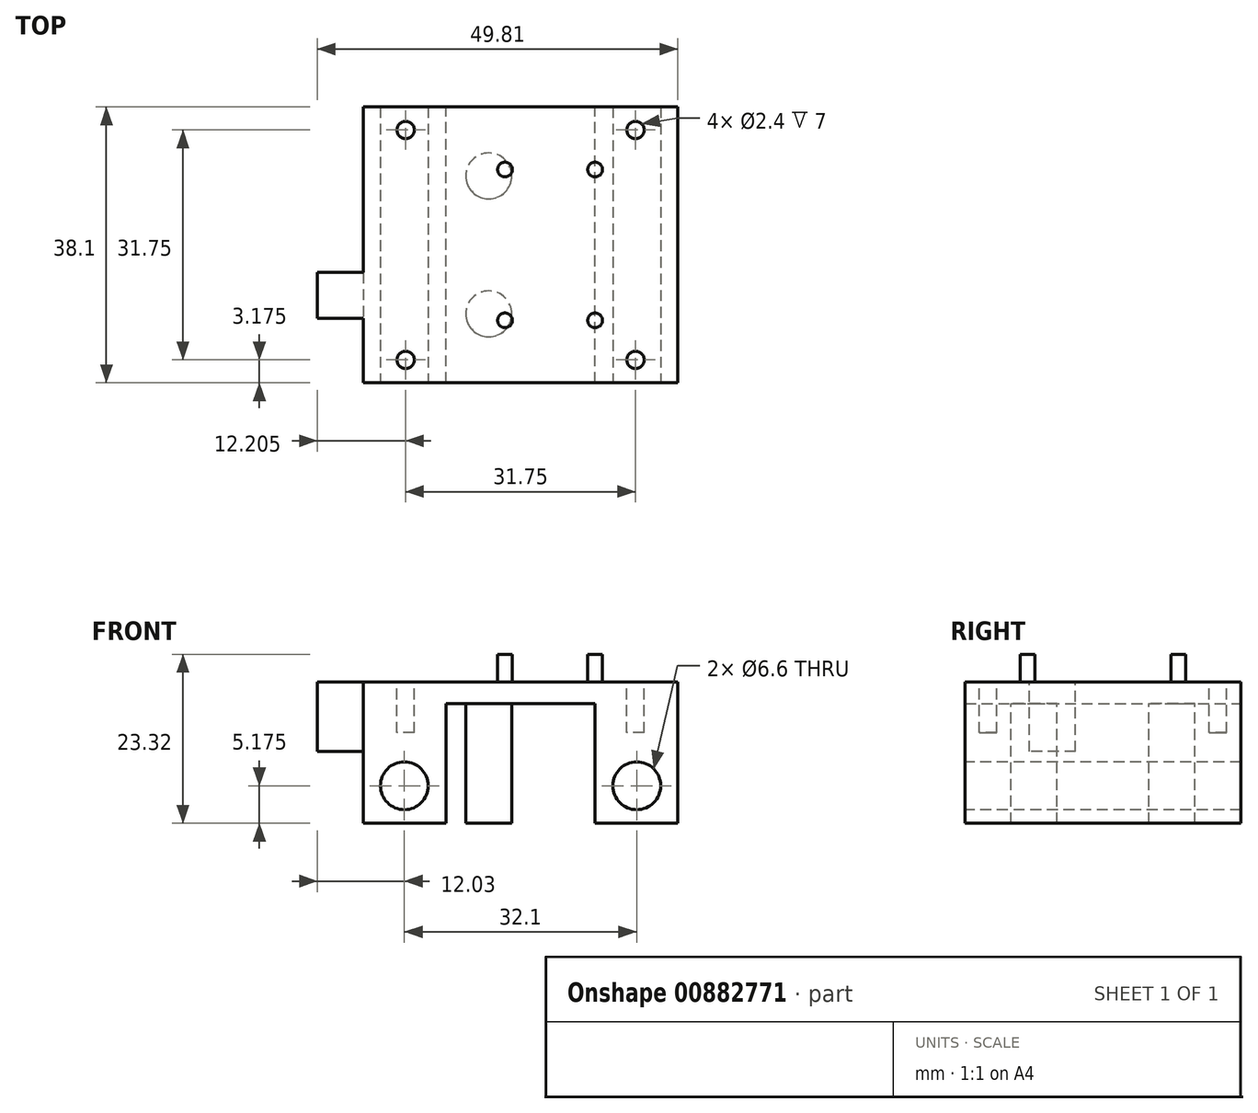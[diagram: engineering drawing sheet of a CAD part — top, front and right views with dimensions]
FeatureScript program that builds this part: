
annotation { "Feature Type Name" : "Feature", "Feature Type Description" : "" }
export const myFeature = defineFeature(function(context is Context, id is Id, definition is map)
    precondition{}
    {
        {
            var Q0;
            Q0=qCreatedBy(makeId("Top.planeOp"),FACE);
            var sketch = newSketch(context, id + "F0", { "sketchPlane" : qUnion([Q0])});
            skLineSegment(sketch, "E0.bottom", {"start": v(21.73, -19.05) * mm, "end": v(-21.73, -19.05) * mm});
            skLineSegment(sketch, "E0.top", {"start": v(21.73, 19.05) * mm, "end": v(-21.73, 19.05) * mm});
            skLineSegment(sketch, "E0.left", {"start": v(21.73, -19.05) * mm, "end": v(21.73, 19.05) * mm});
            skLineSegment(sketch, "E0.right", {"start": v(-21.73, -19.05) * mm, "end": v(-21.73, 19.05) * mm});
            skPoint(sketch, "E0.middle", {"position": v(0, 0) * mm});
            skSolve(sketch);
        }
        {
            var Q0;
            Q0 = qSketchRegion(id + "F0", true);
            extrude(context, id + "F1", {"entities" : qUnion([Q0]), "depth" : 3 * mm, "offsetDistance" : 25.4 * mm});
        }
        {
            var Q0;
            Q0=makeQuery(id+"F1.opExtrude","CAP_FACE",FACE,{"disambiguationData":[OSD([sQuery(id+"F0.wireOp",EDGE,"E0.bottom"),sQuery(id+"F0.wireOp",EDGE,"E0.top"),sQuery(id+"F0.wireOp",EDGE,"E0.left"),sQuery(id+"F0.wireOp",EDGE,"E0.right")])],"isStart":true});
            var sketch = newSketch(context, id + "F2", { "sketchPlane" : qUnion([Q0])});
            skLineSegment(sketch, "E1.bottom", {"start": v(-21.73, 19.05) * mm, "end": v(-10.3, 19.05) * mm});
            skLineSegment(sketch, "E1.top", {"start": v(-21.73, -19.05) * mm, "end": v(-10.3, -19.05) * mm});
            skLineSegment(sketch, "E1.left", {"start": v(-21.73, 19.05) * mm, "end": v(-21.73, -19.05) * mm});
            skLineSegment(sketch, "E1.right", {"start": v(-10.3, 19.05) * mm, "end": v(-10.3, -19.05) * mm});
            skLineSegment(sketch, "E2.MirrorCS", {"start": v(10.3, 19.05) * mm, "end": v(10.3, -19.05) * mm});
            skLineSegment(sketch, "E3.MirrorCS", {"start": v(21.73, 19.05) * mm, "end": v(10.3, 19.05) * mm});
            skLineSegment(sketch, "E4.MirrorCS", {"start": v(21.73, 19.05) * mm, "end": v(21.73, -19.05) * mm});
            skLineSegment(sketch, "E5.MirrorCS", {"start": v(21.73, -19.05) * mm, "end": v(10.3, -19.05) * mm});
            skSolve(sketch);
        }
        {
            var Q0;
            Q0 = qSketchRegion(id + "F2", true);
            extrude(context, id + "F3", {"entities" : qUnion([Q0]), "operationType" : NewBodyOperationType.ADD, "depth" : 16.5 * mm, "offsetDistance" : 25.4 * mm});
        }
        {
            var Q0;
            Q0=makeQuery(id+"F3.boolean.opBoolean","MERGE",FACE,{"derivedFrom":[makeQuery(id+"F1.opExtrude","SWEPT_FACE",FACE,{"disambiguationData":[OSD([sQuery(id+"F0.wireOp",EDGE,"E0.bottom")])]}),makeQuery(id+"F3.opExtrude","SWEPT_FACE",FACE,{"disambiguationData":[OSD([sQuery(id+"F2.wireOp",EDGE,"E1.bottom")])]}),makeQuery(id+"F3.opExtrude","SWEPT_FACE",FACE,{"disambiguationData":[OSD([sQuery(id+"F2.wireOp",EDGE,"E3.MirrorCS")])]})]});
            var sketch = newSketch(context, id + "F4", { "sketchPlane" : qUnion([Q0])});
            skCircle(sketch, "E6", {"center": v(-16.05, -11.34) * mm, "radius": 3.3 * mm});
            skCircle(sketch, "E7.MirrorC", {"center": v(16.05, -11.34) * mm, "radius": 3.3 * mm});
            skSolve(sketch);
        }
        {
            var Q0;
            Q0 = qSketchRegion(id + "F4", true);
            extrude(context, id + "F5", {"entities" : qUnion([Q0]), "operationType" : NewBodyOperationType.REMOVE, "endBound" : BoundingType.UP_TO_NEXT, "oppositeDirection" : true, "depth" : 25.4 * mm, "offsetDistance" : 25.4 * mm});
        }
        {
            var Q0;
            Q0=makeQuery(id+"F1.opExtrude","CAP_FACE",FACE,{"disambiguationData":[OSD([sQuery(id+"F0.wireOp",EDGE,"E0.bottom"),sQuery(id+"F0.wireOp",EDGE,"E0.top"),sQuery(id+"F0.wireOp",EDGE,"E0.left"),sQuery(id+"F0.wireOp",EDGE,"E0.right")])],"isStart":false});
            var sketch = newSketch(context, id + "F6", { "sketchPlane" : qUnion([Q0])});
            skCircle(sketch, "E8", {"center": v(-2.15, -10.41) * mm, "radius": 1.02 * mm});
            skCircle(sketch, "E9", {"center": v(10.3, -10.41) * mm, "radius": 1.02 * mm});
            skCircle(sketch, "E10.MirrorC", {"center": v(-2.15, 10.41) * mm, "radius": 1.02 * mm});
            skCircle(sketch, "E11.MirrorC", {"center": v(10.3, 10.41) * mm, "radius": 1.02 * mm});
            skSolve(sketch);
        }
        {
            var Q0;
            Q0 = qSketchRegion(id + "F6", true);
            extrude(context, id + "F7", {"entities" : qUnion([Q0]), "operationType" : NewBodyOperationType.ADD, "depth" : 3.8 * mm, "offsetDistance" : 25.4 * mm});
        }
        {
            var Q0;
            Q0=makeQuery(id+"F1.opExtrude","CAP_FACE",FACE,{"disambiguationData":[OSD([sQuery(id+"F0.wireOp",EDGE,"E0.bottom"),sQuery(id+"F0.wireOp",EDGE,"E0.top"),sQuery(id+"F0.wireOp",EDGE,"E0.left"),sQuery(id+"F0.wireOp",EDGE,"E0.right")])],"isStart":false});
            var sketch = newSketch(context, id + "F8", { "sketchPlane" : qUnion([Q0])});
            skCircle(sketch, "E12", {"center": v(15.87, 15.87) * mm, "radius": 1.2 * mm});
            skCircle(sketch, "E13", {"center": v(15.87, -15.87) * mm, "radius": 1.2 * mm});
            skCircle(sketch, "E14.MirrorC", {"center": v(-15.87, 15.87) * mm, "radius": 1.2 * mm});
            skCircle(sketch, "E15.MirrorC", {"center": v(-15.87, -15.87) * mm, "radius": 1.2 * mm});
            skSolve(sketch);
        }
        {
            var Q0;
            Q0 = qSketchRegion(id + "F8", true);
            extrude(context, id + "F9", {"entities" : qUnion([Q0]), "operationType" : NewBodyOperationType.REMOVE, "oppositeDirection" : true, "depth" : 7 * mm, "offsetDistance" : 25.4 * mm});
        }
        {
            var Q0;
            Q0=makeQuery(id+"F1.opExtrude","CAP_FACE",FACE,{"disambiguationData":[OSD([sQuery(id+"F0.wireOp",EDGE,"E0.bottom"),sQuery(id+"F0.wireOp",EDGE,"E0.top"),sQuery(id+"F0.wireOp",EDGE,"E0.left"),sQuery(id+"F0.wireOp",EDGE,"E0.right")])],"isStart":true});
            var sketch = newSketch(context, id + "F10", { "sketchPlane" : qUnion([Q0])});
            skCircle(sketch, "E16", {"center": v(-4.39, 9.53) * mm, "radius": 3.18 * mm});
            skCircle(sketch, "E17", {"center": v(-4.39, -9.53) * mm, "radius": 3.18 * mm});
            skSolve(sketch);
        }
        {
            var Q0;
            Q0 = qSketchRegion(id + "F10", true);
            var Q1;
            Q1=makeQuery(id+"F3.opExtrude","CAP_FACE",FACE,{"disambiguationData":[OSD([sQuery(id+"F2.wireOp",EDGE,"E1.bottom"),sQuery(id+"F2.wireOp",EDGE,"E1.top"),sQuery(id+"F2.wireOp",EDGE,"E1.left"),sQuery(id+"F2.wireOp",EDGE,"E1.right")])],"isStart":false});
            extrude(context, id + "F11", {"entities" : qUnion([Q0]), "operationType" : NewBodyOperationType.ADD, "endBound" : BoundingType.UP_TO_SURFACE, "depth" : 25.4 * mm, "endBoundEntityFace" : qUnion([Q1]), "offsetDistance" : 25.4 * mm});
        }
        {
            var Q0;
            Q0=makeQuery(id+"F3.boolean.opBoolean","MERGE",FACE,{"derivedFrom":[makeQuery(id+"F1.opExtrude","SWEPT_FACE",FACE,{"disambiguationData":[OSD([sQuery(id+"F0.wireOp",EDGE,"E0.right")])]}),makeQuery(id+"F3.opExtrude","SWEPT_FACE",FACE,{"disambiguationData":[OSD([sQuery(id+"F2.wireOp",EDGE,"E1.left")])]})]});
            var sketch = newSketch(context, id + "F12", { "sketchPlane" : qUnion([Q0])});
            skLineSegment(sketch, "E18.bottom", {"start": v(3.81, -6.63) * mm, "end": v(10.16, -6.63) * mm});
            skLineSegment(sketch, "E18.top", {"start": v(3.8, 3) * mm, "end": v(10.16, 3) * mm});
            skLineSegment(sketch, "E18.left", {"start": v(10.16, -6.63) * mm, "end": v(10.16, 3) * mm});
            skLineSegment(sketch, "E18.right", {"start": v(3.81, -6.63) * mm, "end": v(3.8, 3) * mm});
            skSolve(sketch);
        }
        {
            var Q0;
            Q0 = qSketchRegion(id + "F12", true);
            extrude(context, id + "F13", {"entities" : qUnion([Q0]), "operationType" : NewBodyOperationType.ADD, "depth" : 6.35 * mm, "offsetDistance" : 25.4 * mm});
        }
    });
